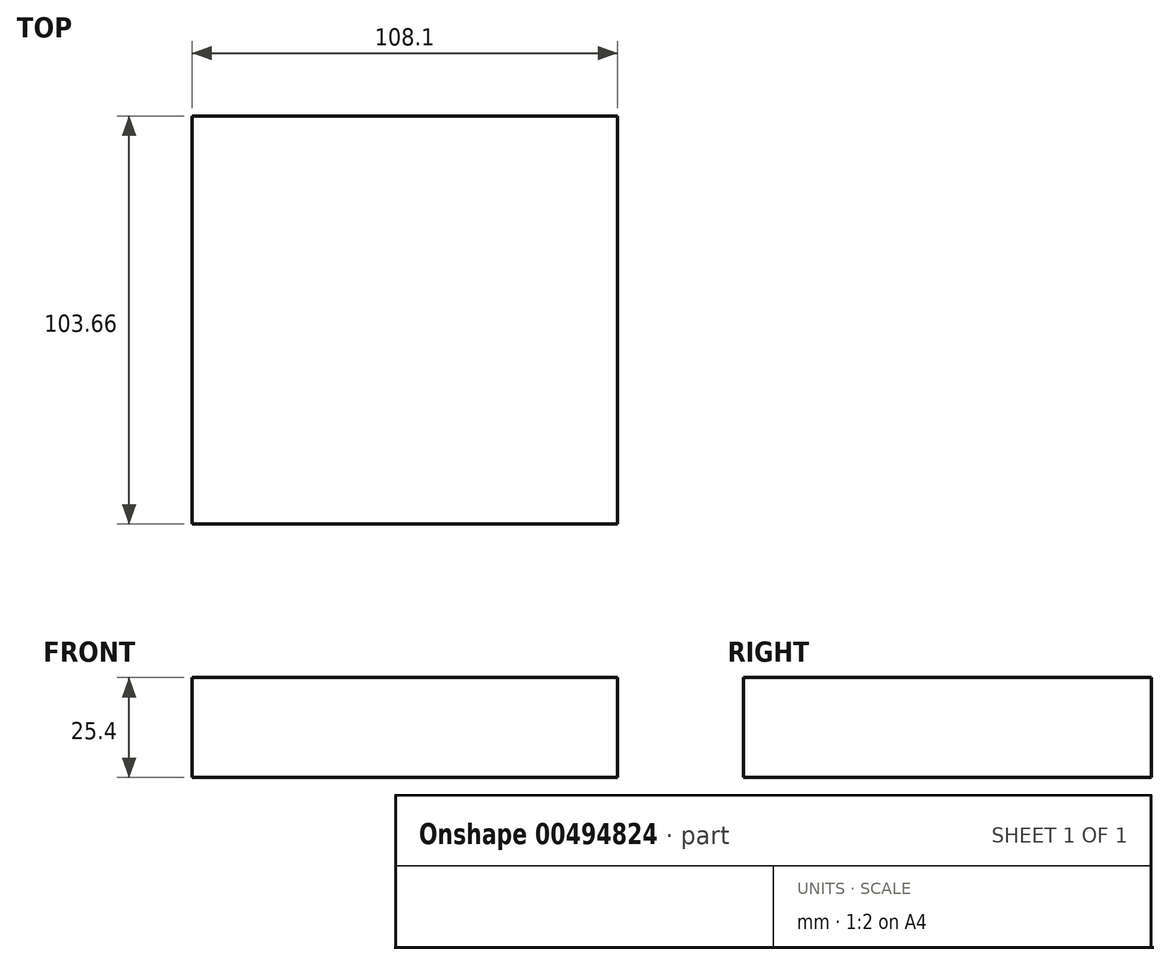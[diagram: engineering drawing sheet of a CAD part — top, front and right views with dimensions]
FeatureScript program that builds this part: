
annotation { "Feature Type Name" : "Feature", "Feature Type Description" : "" }
export const myFeature = defineFeature(function(context is Context, id is Id, definition is map)
    precondition{}
    {
        {
            var Q0;
            Q0=qCreatedBy(makeId("Top.planeOp"),FACE);
            var sketch = newSketch(context, id + "F0", { "sketchPlane" : qUnion([Q0])});
            skLineSegment(sketch, "E0.bottom", {"start": v(53.23, 51.57) * mm, "end": v(-54.87, 51.57) * mm});
            skLineSegment(sketch, "E0.top", {"start": v(53.23, -52.09) * mm, "end": v(-54.87, -52.09) * mm});
            skLineSegment(sketch, "E0.left", {"start": v(53.23, 51.57) * mm, "end": v(53.23, -52.09) * mm});
            skLineSegment(sketch, "E0.right", {"start": v(-54.87, 51.57) * mm, "end": v(-54.87, -52.09) * mm});
            skSolve(sketch);
        }
        {
            var Q0;
            Q0=qCreatedBy(makeId("Top.planeOp"),FACE);
            var sketch = newSketch(context, id + "F1", { "sketchPlane" : qUnion([Q0])});
            skFitSpline(sketch, "E1", {"points": [v(-55.12, 51.4) * mm, v(0, 74.3) * mm, v(53.04, 51.88) * mm], "startDerivative": vector(109.82, 68.26) * mm, "endDerivative": vector(106.48, -67.7) * mm});
            skSolve(sketch);
        }
        {
            var Q0;
            Q0=makeQuery(id+"F0.imprint","IMPRINT",FACE,{"disambiguationData":[TD([[makeQuery(id+"F0.imprint","IMPRINT",EDGE,{"derivedFrom":sQuery(id+"F0.wireOp",EDGE,"E0.bottom")}),1.0]])]});
            var sketch = newSketch(context, id + "F2", { "sketchPlane" : qUnion([Q0])});
            skCircle(sketch, "E2", {"center": v(-39.1, -22.12) * mm, "radius": 11.63 * mm});
            skSolve(sketch);
        }
        {
            var Q0;
            Q0=makeQuery(id+"F0.imprint","IMPRINT",FACE,{"disambiguationData":[TD([[makeQuery(id+"F0.imprint","IMPRINT",EDGE,{"derivedFrom":sQuery(id+"F0.wireOp",EDGE,"E0.bottom")}),1.0]])]});
            extrude(context, id + "F3", {"entities" : qUnion([Q0]), "depth" : 25.4 * mm});
        }
        {
            var Q0;
            Q0=sQuery(id+"F1.wireOp",EDGE,"E1");
            extrude(context, id + "F4", {"bodyType" : ToolBodyType.SURFACE, "surfaceEntities" : qUnion([Q0]), "depth" : 25.4 * mm});
        }
    });
